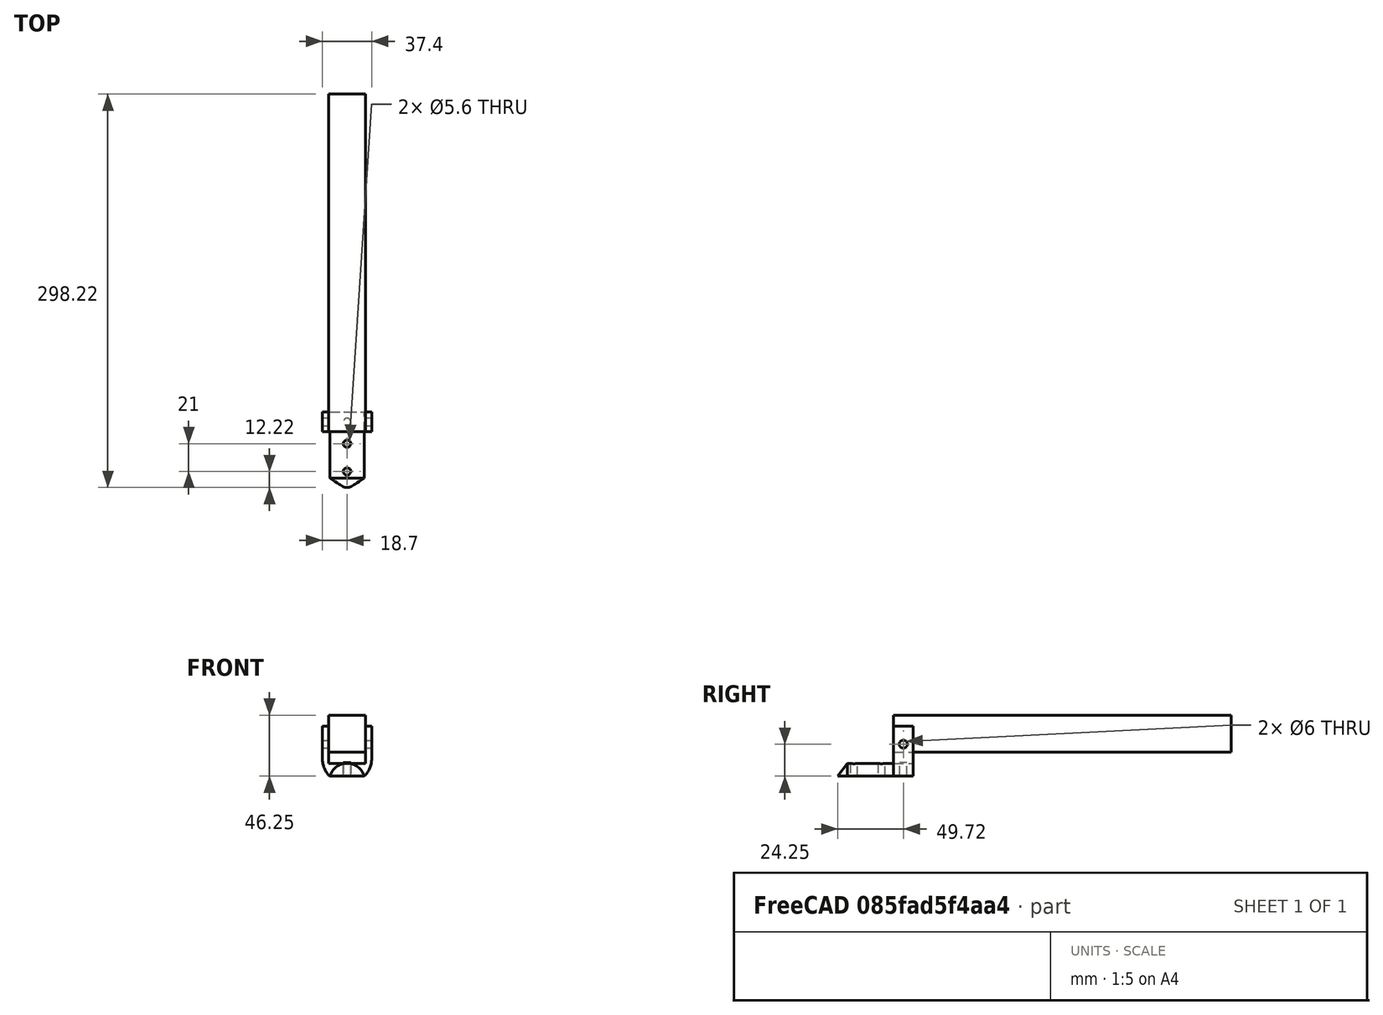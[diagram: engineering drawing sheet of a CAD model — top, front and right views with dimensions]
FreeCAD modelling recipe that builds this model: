
FCSTD DOCUMENT  (FreeCAD 0.20R29410 (Git))
Label: outerLook_Nov_21_2022
License: All rights reserved
LicenseURL: http://en.wikipedia.org/wiki/All_rights_reserved
objects: Part::Cylinder×6, Part::Box×5, Part::Cut×4, Part::MultiFuse×4, Part::Cone×1, Part::MultiCommon×1
note: 21 computed .brp shape members not serialized (recipe doc carries the construction recipe); baked Part::Feature solids carry a one-line shape summary decoded from their .brp

FEATURE [Part::Cylinder] Cylinder
  Angle = 360
  AttacherType = Attacher::AttachEngine3D
  FirstAngle = 0
  Height = 50
  Placement = pos=(13.5,-5,43) rot=(-1,0,0;1.5708rad)
  Radius = 13.5
  SecondAngle = 0
FEATURE [Part::Box] Box  label="TSlotFrameCut"
  AttacherType = Attacher::AttachEngine3D
  Height = 28
  Length = 28
  Placement = pos=(-0.5,30,65) rot=(0,0,1;0rad)
  Width = 256
FEATURE [Part::Box] Box015  label="TSlotMount001"
  AttacherType = Attacher::AttachEngine3D
  Height = 37.75
  Length = 37.4
  Placement = pos=(-5.2,30,46.75) rot=(0,0,1;0rad)
  Width = 15
FEATURE [Part::Cylinder] Cylinder009  label="m5Cut"
  Angle = 360
  AttacherType = Attacher::AttachEngine3D
  FirstAngle = 0
  Height = 100
  Placement = pos=(-56.4,37.5,71) rot=(0,1,0;1.5708rad)
  Radius = 3
  SecondAngle = 0
FEATURE [Part::Box] Box016  label="Shell_Holder002"
  AttacherType = Attacher::AttachEngine3D
  Height = 20
  Length = 27
  Placement = pos=(0,-20.5,26.75) rot=(0,0,1;0rad)
  Width = 75
FEATURE [Part::Cylinder] Cylinder011
  Angle = 360
  AttacherType = Attacher::AttachEngine3D
  FirstAngle = 0
  Height = 12
  Placement = pos=(13.5,0,45) rot=(0,0,1;1.5708rad)
  Radius = 2.8
  SecondAngle = 0
FEATURE [Part::Cylinder] Cylinder012
  Angle = 360
  AttacherType = Attacher::AttachEngine3D
  FirstAngle = 0
  Height = 10
  Placement = pos=(13.5,37.5,47) rot=(0,0,1;1.5708rad)
  Radius = 2.8
  SecondAngle = 0
FEATURE [Part::Box] Box018  label="TSlotFrameCut001"
  AttacherType = Attacher::AttachEngine3D
  Height = 28
  Length = 28
  Placement = pos=(-0.5,0,56.5) rot=(0,0,1;0rad)
  Width = 254
FEATURE [Part::Cut] Cut009  label="TSlotMount002"
  Base = -> Box015
  Tool = -> Box018
FEATURE [Part::Cylinder] Cylinder015
  Angle = 360
  AttacherType = Attacher::AttachEngine3D
  FirstAngle = 0
  Height = 12
  Placement = pos=(13.5,21,45) rot=(0,0,1;1.5708rad)
  Radius = 2.8
  SecondAngle = 0
FEATURE [Part::Cone] Cone
  Angle = 180
  AttacherType = Attacher::AttachEngine3D
  Height = 10
  Placement = pos=(13.5,-5,43) rot=(1,0,0;1.5708rad)
  Radius1 = 13.5
  Radius2 = 0
FEATURE [Part::MultiFuse] Fusion  label="beak"
  Shapes = -> [Cylinder,Cone]
FEATURE [Part::Cut] Cut
  Base = -> Fusion
  Tool = -> Box016
FEATURE [Part::MultiFuse] Fusion001  label="heatSetCuts"
  Shapes = -> [Cylinder011,Cylinder015]
FEATURE [Part::Cut] Cut010
  Base = -> Cut009
  Tool = -> Cylinder009
FEATURE [Part::MultiFuse] Fusion002
  Shapes = -> [Cut,Cut010]
FEATURE [Part::Cut] Cut011
  Base = -> Fusion002
  Tool = -> Fusion001
FEATURE [Part::Cylinder] Cylinder016  label="reshapes"
  Angle = 360
  AttacherType = Attacher::AttachEngine3D
  FirstAngle = 0
  Height = 63
  Placement = pos=(13.5,45,60) rot=(1,0,0;1.5708rad)
  Radius = 18.7
  SecondAngle = 0
FEATURE [Part::Box] Box019  label="reshapes001"
  AttacherType = Attacher::AttachEngine3D
  Height = 29
  Length = 40
  Placement = pos=(-6.5,30,60) rot=(0,0,1;0rad)
  Width = 18
FEATURE [Part::MultiFuse] Fusion003
  Shapes = -> [Box019,Cylinder016]
FEATURE [Part::MultiCommon] Common
  Shapes = -> [Fusion003,Cut011]
